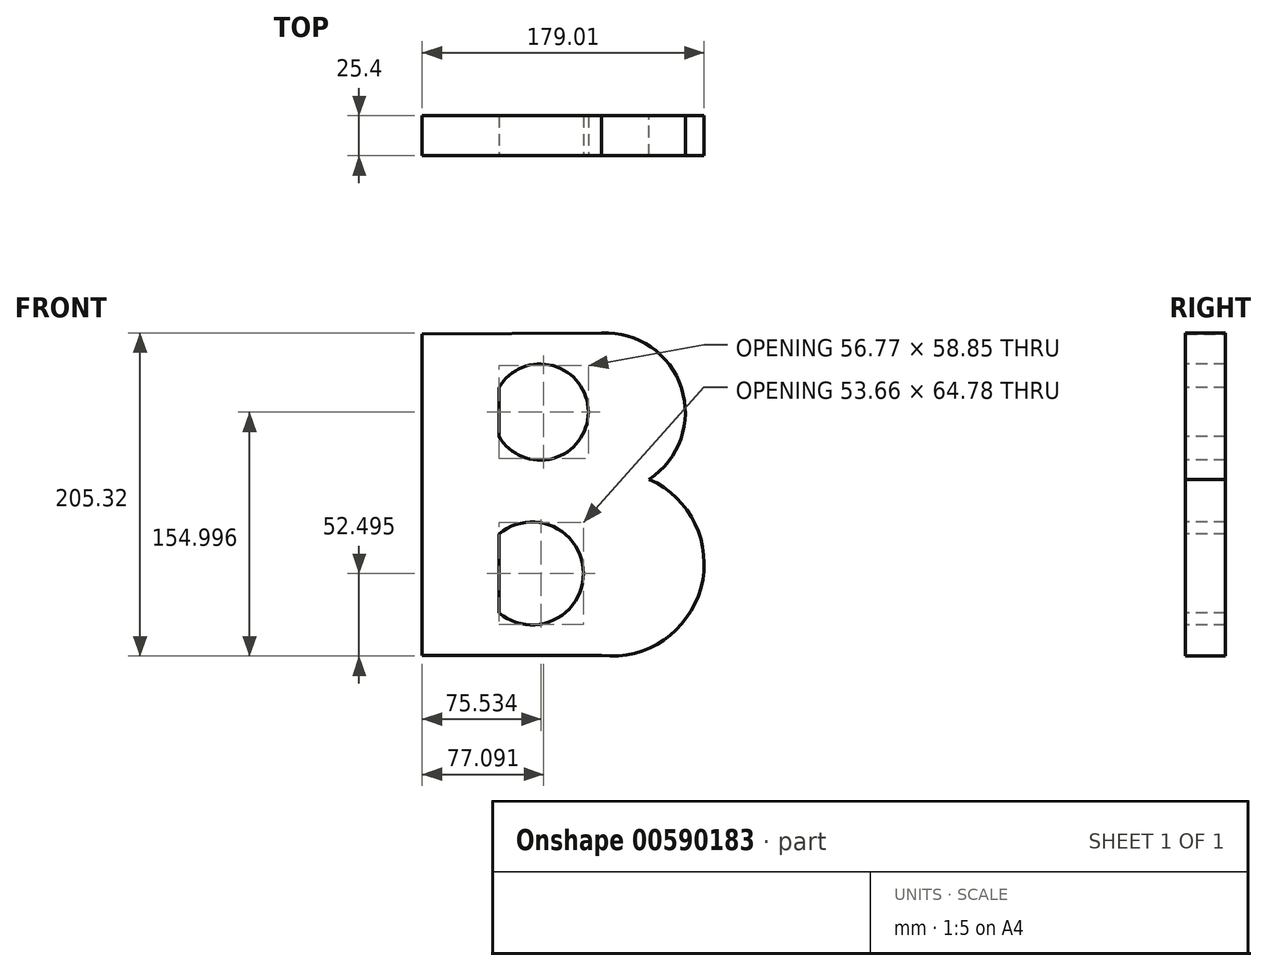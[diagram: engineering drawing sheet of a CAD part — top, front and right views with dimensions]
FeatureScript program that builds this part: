
annotation { "Feature Type Name" : "Feature", "Feature Type Description" : "" }
export const myFeature = defineFeature(function(context is Context, id is Id, definition is map)
    precondition{}
    {
        {
            var Q0;
            Q0=qCreatedBy(makeId("Front.planeOp"),FACE);
            var sketch = newSketch(context, id + "F0", { "sketchPlane" : qUnion([Q0])});
            skLineSegment(sketch, "E0", {"start": v(-113.88, 51.74) * mm, "end": v(-113.88, -152.55) * mm});
            skLineSegment(sketch, "E1", {"start": v(-113.88, -152.55) * mm, "end": v(0, -152.55) * mm});
            skArc(sketch, "E2", {"start": v(0, -152.55) * mm, "mid": v(63.1, -109.53) * mm, "end": v(30.25, -40.58) * mm});
            skArc(sketch, "E3", {"start": v(30.25, -40.58) * mm, "mid": v(50.73, 17.47) * mm, "end": v(0, 52.34) * mm});
            skLineSegment(sketch, "E4", {"start": v(-113.88, 51.74) * mm, "end": v(0, 52.34) * mm});
            skSolve(sketch);
        }
        {
            var Q0;
            Q0=makeQuery(id+"F0.imprint","IMPRINT",FACE,{"disambiguationData":[TD([[makeQuery(id+"F0.imprint","IMPRINT",EDGE,{"derivedFrom":sQuery(id+"F0.wireOp",EDGE,"E0")}),1.0]])]});
            extrude(context, id + "F1", {"entities" : qUnion([Q0]), "depth" : 25.4 * mm, "offsetDistance" : 25.4 * mm});
        }
        {
            var Q0;
            Q0=makeQuery(id+"F1.opExtrude","CAP_FACE",FACE,{"disambiguationData":[OSD([sQuery(id+"F0.wireOp",EDGE,"E0"),sQuery(id+"F0.wireOp",EDGE,"E1"),sQuery(id+"F0.wireOp",EDGE,"E2"),sQuery(id+"F0.wireOp",EDGE,"E3"),sQuery(id+"F0.wireOp",EDGE,"E4")])],"isStart":false});
            var sketch = newSketch(context, id + "F2", { "sketchPlane" : qUnion([Q0])});
            skLineSegment(sketch, "E5", {"start": v(-65.17, 17.58) * mm, "end": v(-65.17, -13.41) * mm});
            skArc(sketch, "E6", {"start": v(-65.17, -13.41) * mm, "mid": v(-8.4, 2.09) * mm, "end": v(-65.17, 17.58) * mm});
            skLineSegment(sketch, "E7", {"start": v(-65.17, -75.38) * mm, "end": v(-65.17, -125.45) * mm});
            skArc(sketch, "E8", {"start": v(-65.17, -125.45) * mm, "mid": v(-11.52, -100.42) * mm, "end": v(-65.17, -75.38) * mm});
            skSolve(sketch);
        }
        {
            var Q0;
            Q0 = qSketchRegion(id + "F2", true);
            extrude(context, id + "F3", {"entities" : qUnion([Q0]), "operationType" : NewBodyOperationType.REMOVE, "oppositeDirection" : true, "depth" : 25.4 * mm, "offsetDistance" : 25.4 * mm});
        }
    });
